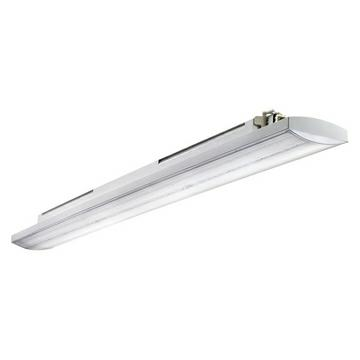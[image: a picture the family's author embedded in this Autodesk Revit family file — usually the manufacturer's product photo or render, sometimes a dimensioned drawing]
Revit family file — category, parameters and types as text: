
# Revit family: Lighting-Industrial-GEWISS-SMART[3]PLUS-HLO-WATERTIGHT-LED_TRANSPARENT_MEDBEAM_1600mm
name_source: partatom
category: Apparecchi per illuminazione
units: mm (PartAtom-declared; Revit-internal decimal feet)

## family parameters
Condiviso = No
Host = Superficie
Punto di calcolo locali = No
Quota connettore circolare = Usa diametro
Sorgente d'illuminazione = Sì
Taglio con vuoti quando caricato = No
Tipo di parte = Normale

## types (1)
- Lighting-Industrial-GEWISS-SMART[3]PLUS-HLO-WATERTIGHT-LED_TRANSPARENT_MEDBEAM_1600mm
    Angolo inclinazione = -90.00°
    Application = Indoor
    Carico apparente = 67 VA
    Catalogue = LIGHTING
    Catalogue Range = SMART[3] PLUS HLO
    Colour temperature = 5700 K (CRI > 90)
    Colour temperature: = 5700 K (CRI > 90)
    Commenti sul wattaggio = 67W
    Descrizione = SMART3 PLUS 1600 T.W.DALI HO CONC 9 57
    Efficiency class of integrated LEDs = A ÷ A++
    Electrocod = 2434
    Emetti da lunghezza linea = 1200 mm
    File diagramma fotometrico = GWS3323BC957.IES
    Filtro dei colori = 16777215
    Ganci = Alluminio
    Glow Wire Test = 850°C
    IDF = 2e32ed57-e4cd-4863-9dd7-ff54225198b2
    IDT = b00432e8-6c7e-4c0b-b2bb-cd3ca21adb70
    IP degree = IP66/IP69
    Immagine tipo = GWS3280TS.jpg
    Insulation class = II
    Lamp = LED
    Lampada = LED
    Length = 1600 mm
    Lumen output (lm) = 7100
    Lunghezza Lampada = 1600 mm  [stored 5.24934 ft]
    Modello = GWS3323BC957
    Numero poli = 2
    Operating temperature: = -25 +45 °C
    Produttore = GEWISS S.p.A.
    Prospetto di default = 1219 mm
    SEO = Ceiling
    Schermo. = Led Acceso
    Shield type = Transparent
    Shock resistance = IK08
    Stampa 1_100 = Sì
    Stampa 1_200 = No
    Struttura = GRIGIO
    System power = 63 W
    Technical sheet = https://www.gewiss.com
    Type of light source = LED - Not replaceable
    Typology = DALI
    URL = https://www.gewiss.com
    Variazione temperatura colore lampada con luminosità attenuata = <Nessuno>
    Version file RFA = 20.0
    Voltage = 220-240 V
    Warranty = 5 years
    Working temperature = -25 +45 °C

note: [stored X ft] marks values corroborated as IEEE doubles in the binary element streams (Revit-internal decimal feet)
